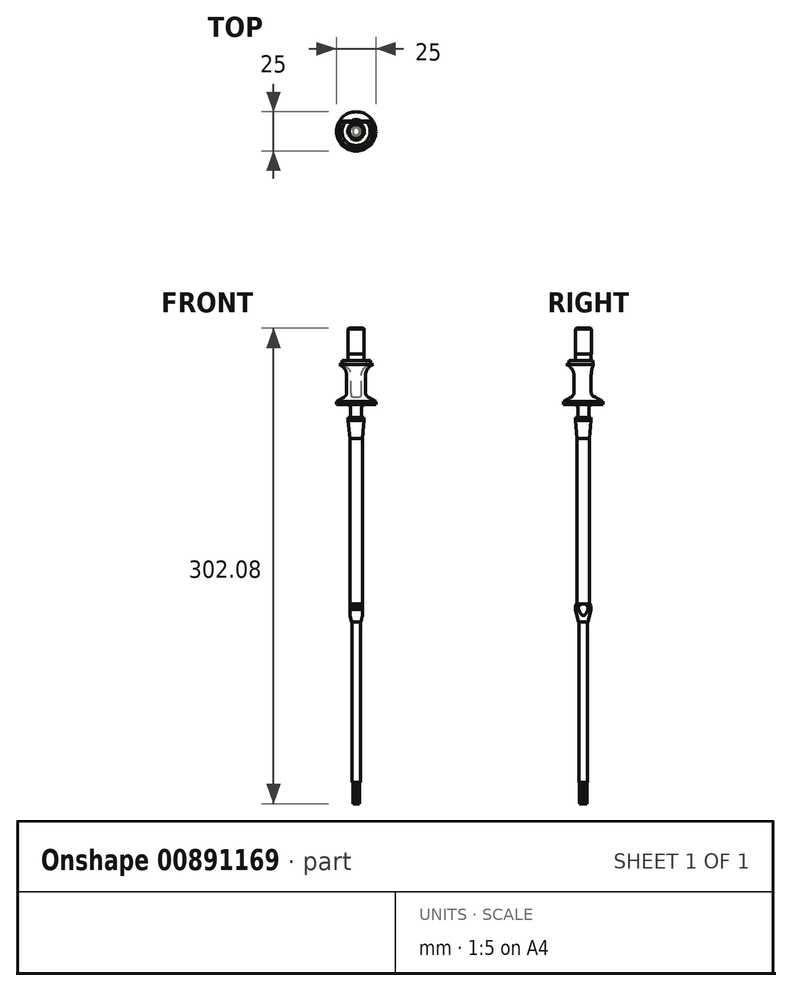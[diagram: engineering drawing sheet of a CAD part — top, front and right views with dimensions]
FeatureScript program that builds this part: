
annotation { "Feature Type Name" : "Feature", "Feature Type Description" : "" }
export const myFeature = defineFeature(function(context is Context, id is Id, definition is map)
    precondition{}
    {
        {
            var Q0;
            Q0=qCreatedBy(makeId("Front.planeOp"),FACE);
            var sketch = newSketch(context, id + "F0", { "sketchPlane" : qUnion([Q0])});
            skLineSegment(sketch, "E0.bottom", {"start": v(0, 218.5) * mm, "end": v(4, 218.5) * mm});
            skLineSegment(sketch, "E0.top", {"start": v(0, 113.5) * mm, "end": v(4, 113.5) * mm});
            skLineSegment(sketch, "E0.left", {"start": v(0, 218.5) * mm, "end": v(0, 113.5) * mm});
            skLineSegment(sketch, "E0.right", {"start": v(4, 218.5) * mm, "end": v(4, 113.5) * mm});
            skLineSegment(sketch, "E1", {"start": v(0, 230) * mm, "end": v(5, 230) * mm});
            skLineSegment(sketch, "E2", {"start": v(4, 218.5) * mm, "end": v(5, 230) * mm});
            skLineSegment(sketch, "E3", {"start": v(0, 230) * mm, "end": v(0, 218.5) * mm});
            skLineSegment(sketch, "E4", {"start": v(0, 112) * mm, "end": v(5, 112) * mm});
            skLineSegment(sketch, "E5", {"start": v(0, 113.5) * mm, "end": v(0, 112) * mm});
            skLineSegment(sketch, "E6", {"start": v(5, 112) * mm, "end": v(5, 110) * mm});
            skLineSegment(sketch, "E7", {"start": v(4, 113.5) * mm, "end": v(5, 112) * mm});
            skLineSegment(sketch, "E8", {"start": v(0, 112) * mm, "end": v(0, 110) * mm});
            skLineSegment(sketch, "E9", {"start": v(0, 110) * mm, "end": v(5, 110) * mm});
            skLineSegment(sketch, "E10", {"start": v(0, 110) * mm, "end": v(0, 102) * mm});
            skLineSegment(sketch, "E11", {"start": v(0, 102) * mm, "end": v(3, 102) * mm});
            skLineSegment(sketch, "E12", {"start": v(5, 110) * mm, "end": v(3, 102) * mm});
            skLineSegment(sketch, "E13.bottom", {"start": v(0, 102) * mm, "end": v(2.7, 102) * mm});
            skLineSegment(sketch, "E13.top", {"start": v(0, 0) * mm, "end": v(2.7, 0) * mm});
            skLineSegment(sketch, "E13.left", {"start": v(0, 102) * mm, "end": v(0, 0) * mm});
            skLineSegment(sketch, "E13.right", {"start": v(2.7, 102) * mm, "end": v(2.7, 0) * mm});
            skLineSegment(sketch, "E14.top", {"start": v(0, 232) * mm, "end": v(5, 232) * mm});
            skLineSegment(sketch, "E14.left", {"start": v(0, 230) * mm, "end": v(0, 232) * mm});
            skLineSegment(sketch, "E14.right", {"start": v(5, 230) * mm, "end": v(5, 232) * mm});
            skLineSegment(sketch, "E15.bottom", {"start": v(0, 232) * mm, "end": v(3.5, 232) * mm});
            skLineSegment(sketch, "E15.top", {"start": v(0, 238) * mm, "end": v(3.5, 238) * mm});
            skLineSegment(sketch, "E15.left", {"start": v(0, 232) * mm, "end": v(0, 238) * mm});
            skLineSegment(sketch, "E15.right", {"start": v(3.5, 232) * mm, "end": v(3.5, 238) * mm});
            skLineSegment(sketch, "E16", {"start": v(0, 238) * mm, "end": v(0, 240) * mm});
            skLineSegment(sketch, "E17", {"start": v(0, 240) * mm, "end": v(12.5, 240) * mm});
            skLineSegment(sketch, "E18", {"start": v(12.5, 240) * mm, "end": v(12.5, 242) * mm});
            skLineSegment(sketch, "E19", {"start": v(12.5, 242) * mm, "end": v(0, 242) * mm});
            skLineSegment(sketch, "E20", {"start": v(0, 242) * mm, "end": v(0, 240) * mm});
            skLineSegment(sketch, "E21", {"start": v(0, 242) * mm, "end": v(0, 245) * mm});
            skLineSegment(sketch, "E22", {"start": v(0, 245) * mm, "end": v(7.46, 245) * mm});
            skLineSegment(sketch, "E23", {"start": v(7.46, 245) * mm, "end": v(12.5, 242) * mm});
            skLineSegment(sketch, "E24", {"start": v(0, 245) * mm, "end": v(0, 247.58) * mm});
            skLineSegment(sketch, "E25", {"start": v(0, 247.58) * mm, "end": v(6, 247.58) * mm});
            skLineSegment(sketch, "E26.top", {"start": v(0, 258.58) * mm, "end": v(6, 258.58) * mm});
            skLineSegment(sketch, "E26.left", {"start": v(0, 247.58) * mm, "end": v(0, 258.58) * mm});
            skLineSegment(sketch, "E26.right", {"start": v(6, 247.58) * mm, "end": v(6, 258.58) * mm});
            skLineSegment(sketch, "E27", {"start": v(0, 258.58) * mm, "end": v(0, 265.58) * mm});
            skLineSegment(sketch, "E28", {"start": v(0, 265.58) * mm, "end": v(11, 265.58) * mm});
            skArc(sketch, "E29", {"start": v(11, 265.58) * mm, "mid": v(7.38, 262.88) * mm, "end": v(6, 258.58) * mm});
            skArc(sketch, "E30", {"start": v(5.5, 240) * mm, "mid": v(4.09, 239.41) * mm, "end": v(3.5, 238) * mm});
            skArc(sketch, "E31", {"start": v(6, 247.58) * mm, "mid": v(6.4, 246.1) * mm, "end": v(7.46, 245) * mm});
            skLineSegment(sketch, "E32.bottom", {"start": v(0, 265.58) * mm, "end": v(8.98, 265.58) * mm});
            skLineSegment(sketch, "E32.top", {"start": v(0, 268.08) * mm, "end": v(8.98, 268.08) * mm});
            skLineSegment(sketch, "E32.left", {"start": v(0, 265.58) * mm, "end": v(0, 268.08) * mm});
            skLineSegment(sketch, "E32.right", {"start": v(8.98, 265.58) * mm, "end": v(8.98, 268.08) * mm});
            skLineSegment(sketch, "E33.bottom", {"start": v(0, 268.08) * mm, "end": v(5, 268.08) * mm});
            skLineSegment(sketch, "E33.top", {"start": v(0, 272.08) * mm, "end": v(5, 272.08) * mm});
            skLineSegment(sketch, "E33.left", {"start": v(0, 268.08) * mm, "end": v(0, 272.08) * mm});
            skLineSegment(sketch, "E33.right", {"start": v(5, 268.08) * mm, "end": v(5, 272.08) * mm});
            skLineSegment(sketch, "E34.bottom", {"start": v(0, 272.08) * mm, "end": v(5.13, 272.08) * mm});
            skLineSegment(sketch, "E34.top", {"start": v(0, 288.08) * mm, "end": v(5.13, 288.08) * mm});
            skLineSegment(sketch, "E34.left", {"start": v(0, 272.08) * mm, "end": v(0, 288.08) * mm});
            skLineSegment(sketch, "E34.right", {"start": v(5.13, 272.08) * mm, "end": v(5.13, 288.08) * mm});
            skLineSegment(sketch, "E35", {"start": v(0, 288.08) * mm, "end": v(0, 288.58) * mm});
            skLineSegment(sketch, "E36", {"start": v(0, 288.58) * mm, "end": v(4.5, 288.58) * mm});
            skLineSegment(sketch, "E37", {"start": v(4.5, 288.58) * mm, "end": v(5.12, 288.08) * mm});
            skSolve(sketch);
        }
        {
            var Q0;
            Q0 = qSketchRegion(id + "F0", true);
            var Q1;
            Q1=sQuery(id+"F0.wireOp",EDGE,"E0.left");
            revolve(context, id + "F1", {"surfaceOperationType" : NewSurfaceOperationType.NEW, "entities" : qUnion([Q0]), "axis" : qUnion([Q1]), "revolveType" : RevolveType.FULL});
        }
        {
            var Q0;
            Q0=qCreatedBy(makeId("Front.planeOp"),FACE);
            var sketch = newSketch(context, id + "F2", { "sketchPlane" : qUnion([Q0])});
            skLineSegment(sketch, "E38.bottom", {"start": v(-4, 113.5) * mm, "end": v(-8, 113.5) * mm});
            skLineSegment(sketch, "E38.top", {"start": v(-4, 102) * mm, "end": v(-8, 102) * mm});
            skLineSegment(sketch, "E38.left", {"start": v(-4, 113.5) * mm, "end": v(-4, 102) * mm});
            skLineSegment(sketch, "E38.right", {"start": v(-8, 113.5) * mm, "end": v(-8, 102) * mm});
            skLineSegment(sketch, "E39.bottom", {"start": v(4, 113.5) * mm, "end": v(8, 113.5) * mm});
            skLineSegment(sketch, "E39.top", {"start": v(4, 102) * mm, "end": v(8, 102) * mm});
            skLineSegment(sketch, "E39.left", {"start": v(4, 113.5) * mm, "end": v(4, 102) * mm});
            skLineSegment(sketch, "E39.right", {"start": v(8, 113.5) * mm, "end": v(8, 102) * mm});
            skLineSegment(sketch, "E40", {"start": v(-4, 113.5) * mm, "end": v(-4, 218.5) * mm});
            skLineSegment(sketch, "E41", {"start": v(-4, 218.5) * mm, "end": v(-5, 230) * mm});
            skLineSegment(sketch, "E42.0", {"start": v(-4, 218.5) * mm, "end": v(4, 218.5) * mm});
            skLineSegment(sketch, "E43", {"start": v(-5, 110) * mm, "end": v(-5, 112) * mm});
            skSolve(sketch);
        }
        {
            var Q0;
            Q0=makeQuery(id+"F2.imprint","IMPRINT",FACE,{"disambiguationData":[TD([[makeQuery(id+"F2.imprint","IMPRINT",EDGE,{"derivedFrom":sQuery(id+"F2.wireOp",EDGE,"E38.bottom")}),1.0]])]});
            var Q1;
            Q1=makeQuery(id+"F2.imprint","IMPRINT",FACE,{"disambiguationData":[TD([[makeQuery(id+"F2.imprint","IMPRINT",EDGE,{"derivedFrom":sQuery(id+"F2.wireOp",EDGE,"E39.bottom")}),-1.0]])]});
            extrude(context, id + "F3", {"entities" : qUnion([Q0, Q1]), "operationType" : NewBodyOperationType.REMOVE, "oppositeDirection" : true, "depth" : 25 * mm, "offsetDistance" : 25 * mm, "hasSecondDirection" : true, "secondDirectionOppositeDirection" : false, "secondDirectionDepth" : 25 * mm});
        }
        {
            var Q0;
            Q0=qCreatedBy(makeId("Right.planeOp"),FACE);
            var sketch = newSketch(context, id + "F4", { "sketchPlane" : qUnion([Q0])});
            skLineSegment(sketch, "E44.bottom", {"start": v(6, 258.58) * mm, "end": v(5, 258.58) * mm});
            skLineSegment(sketch, "E44.top", {"start": v(6, 247.58) * mm, "end": v(5, 247.58) * mm});
            skLineSegment(sketch, "E44.left", {"start": v(6, 258.58) * mm, "end": v(6, 247.58) * mm});
            skLineSegment(sketch, "E44.right", {"start": v(5, 258.58) * mm, "end": v(5, 247.58) * mm});
            skLineSegment(sketch, "E45", {"start": v(0, 0) * mm, "end": v(0, 308.45) * mm, "construction": true});
            skArc(sketch, "E46", {"start": v(6.5, 265.58) * mm, "mid": v(5.38, 262.16) * mm, "end": v(5, 258.58) * mm});
            skLineSegment(sketch, "E47", {"start": v(6.5, 265.58) * mm, "end": v(13.4, 265.58) * mm});
            skLineSegment(sketch, "E48", {"start": v(13.4, 265.58) * mm, "end": v(7.46, 259.96) * mm});
            skLineSegment(sketch, "E49.bottom", {"start": v(0, 218.5) * mm, "end": v(4, 218.5) * mm});
            skLineSegment(sketch, "E49.top", {"start": v(0, 113.5) * mm, "end": v(4, 113.5) * mm});
            skLineSegment(sketch, "E49.left", {"start": v(0, 218.5) * mm, "end": v(0, 113.5) * mm});
            skLineSegment(sketch, "E49.right", {"start": v(4, 218.5) * mm, "end": v(4, 113.5) * mm});
            skLineSegment(sketch, "E50", {"start": v(0, 230) * mm, "end": v(5, 230) * mm});
            skLineSegment(sketch, "E51", {"start": v(4, 218.5) * mm, "end": v(5, 230) * mm});
            skLineSegment(sketch, "E52", {"start": v(0, 230) * mm, "end": v(0, 218.5) * mm});
            skLineSegment(sketch, "E53", {"start": v(0, 112) * mm, "end": v(5, 112) * mm});
            skLineSegment(sketch, "E54", {"start": v(0, 113.5) * mm, "end": v(0, 112) * mm});
            skLineSegment(sketch, "E55", {"start": v(5, 112) * mm, "end": v(5, 110) * mm});
            skLineSegment(sketch, "E56", {"start": v(4, 113.5) * mm, "end": v(5, 112) * mm});
            skLineSegment(sketch, "E57", {"start": v(0, 112) * mm, "end": v(0, 110) * mm});
            skLineSegment(sketch, "E58", {"start": v(0, 110) * mm, "end": v(5, 110) * mm});
            skLineSegment(sketch, "E59", {"start": v(0, 110) * mm, "end": v(0, 102) * mm});
            skLineSegment(sketch, "E60", {"start": v(0, 102) * mm, "end": v(3, 102) * mm});
            skLineSegment(sketch, "E61", {"start": v(5, 110) * mm, "end": v(3, 102) * mm});
            skLineSegment(sketch, "E62.top", {"start": v(0, 0) * mm, "end": v(3, 0) * mm});
            skLineSegment(sketch, "E62.left", {"start": v(0, 102) * mm, "end": v(0, 0) * mm});
            skLineSegment(sketch, "E62.right", {"start": v(3, 102) * mm, "end": v(3, 0) * mm});
            skLineSegment(sketch, "E63.top", {"start": v(0, 232) * mm, "end": v(5, 232) * mm});
            skLineSegment(sketch, "E63.left", {"start": v(0, 230) * mm, "end": v(0, 232) * mm});
            skLineSegment(sketch, "E63.right", {"start": v(5, 230) * mm, "end": v(5, 232) * mm});
            skLineSegment(sketch, "E64.bottom", {"start": v(0, 232) * mm, "end": v(3.5, 232) * mm});
            skLineSegment(sketch, "E64.top", {"start": v(0, 238) * mm, "end": v(3.5, 238) * mm});
            skLineSegment(sketch, "E64.left", {"start": v(0, 232) * mm, "end": v(0, 238) * mm});
            skLineSegment(sketch, "E64.right", {"start": v(3.5, 232) * mm, "end": v(3.5, 238) * mm});
            skLineSegment(sketch, "E65", {"start": v(0, 238) * mm, "end": v(0, 240) * mm});
            skLineSegment(sketch, "E66", {"start": v(0, 240) * mm, "end": v(12.5, 240) * mm});
            skLineSegment(sketch, "E67", {"start": v(12.5, 240) * mm, "end": v(12.5, 242) * mm});
            skLineSegment(sketch, "E68", {"start": v(12.5, 242) * mm, "end": v(0, 242) * mm});
            skLineSegment(sketch, "E69", {"start": v(0, 242) * mm, "end": v(0, 240) * mm});
            skLineSegment(sketch, "E70", {"start": v(0, 242) * mm, "end": v(0, 245) * mm});
            skLineSegment(sketch, "E71", {"start": v(0, 245) * mm, "end": v(7.46, 245) * mm});
            skLineSegment(sketch, "E72", {"start": v(7.46, 245) * mm, "end": v(12.5, 242) * mm});
            skLineSegment(sketch, "E73", {"start": v(0, 245) * mm, "end": v(0, 247.58) * mm});
            skLineSegment(sketch, "E74", {"start": v(0, 247.58) * mm, "end": v(6, 247.58) * mm});
            skLineSegment(sketch, "E75.top", {"start": v(0, 258.58) * mm, "end": v(6, 258.58) * mm});
            skLineSegment(sketch, "E75.left", {"start": v(0, 247.58) * mm, "end": v(0, 258.58) * mm});
            skLineSegment(sketch, "E75.right", {"start": v(6, 247.58) * mm, "end": v(6, 258.58) * mm});
            skLineSegment(sketch, "E76", {"start": v(0, 258.58) * mm, "end": v(0, 265.58) * mm});
            skLineSegment(sketch, "E77", {"start": v(0, 265.58) * mm, "end": v(11, 265.58) * mm});
            skArc(sketch, "E78", {"start": v(11, 265.58) * mm, "mid": v(7.38, 262.88) * mm, "end": v(6, 258.58) * mm});
            skLineSegment(sketch, "E79.bottom", {"start": v(0, 265.58) * mm, "end": v(3.5, 265.58) * mm});
            skLineSegment(sketch, "E79.top", {"start": v(0, 280.58) * mm, "end": v(3.5, 280.58) * mm});
            skLineSegment(sketch, "E79.left", {"start": v(0, 265.58) * mm, "end": v(0, 280.58) * mm});
            skLineSegment(sketch, "E79.right", {"start": v(3.5, 265.58) * mm, "end": v(3.5, 280.58) * mm});
            skArc(sketch, "E80", {"start": v(5.5, 240) * mm, "mid": v(4.09, 239.41) * mm, "end": v(3.5, 238) * mm});
            skArc(sketch, "E81", {"start": v(6, 247.58) * mm, "mid": v(6.4, 246.1) * mm, "end": v(7.46, 245) * mm});
            skArc(sketch, "E82", {"start": v(5, 247.58) * mm, "mid": v(5.72, 245.8) * mm, "end": v(7.46, 245) * mm});
            skLineSegment(sketch, "E83", {"start": v(7.46, 245) * mm, "end": v(7.46, 259.96) * mm});
            skLineSegment(sketch, "E84.bottom", {"start": v(6.5, 265.58) * mm, "end": v(11.23, 265.58) * mm});
            skLineSegment(sketch, "E84.top", {"start": v(6.5, 269.27) * mm, "end": v(11.23, 269.27) * mm});
            skLineSegment(sketch, "E84.left", {"start": v(6.5, 265.58) * mm, "end": v(6.5, 269.27) * mm, "construction": true});
            skLineSegment(sketch, "E84.right", {"start": v(11.23, 265.58) * mm, "end": v(11.23, 269.27) * mm});
            skLineSegment(sketch, "E85.top", {"start": v(6.5, 265.58) * mm, "end": v(6, 265.58) * mm});
            skLineSegment(sketch, "E86.top", {"start": v(6.5, 269.27) * mm, "end": v(6, 269.27) * mm});
            skLineSegment(sketch, "E86.left", {"start": v(6.5, 265.58) * mm, "end": v(6.5, 269.27) * mm});
            skLineSegment(sketch, "E86.right", {"start": v(6, 265.58) * mm, "end": v(6, 269.27) * mm});
            skSolve(sketch);
        }
        {
            var Q0;
            {var subQ5=sQuery(id+"F4.wireOp",EDGE,"E78");Q0=makeQuery(id+"F4.imprint","IMPRINT",FACE,{"disambiguationData":[TD([[makeQuery(id+"F4.imprint","IMPRINT",EDGE,{"derivedFrom":subQ5}),-1.0]])]});}
            var Q1;
            {var subQ0=sQuery(id+"F4.wireOp",EDGE,"E44.right");Q1=makeQuery(id+"F4.imprint","IMPRINT",FACE,{"disambiguationData":[TD([[makeQuery(id+"F4.imprint","IMPRINT",EDGE,{"derivedFrom":subQ0}),1.0]])]});}
            var Q2;
            {var subQ2=sQuery(id+"F4.wireOp",EDGE,"E81");Q2=makeQuery(id+"F4.imprint","IMPRINT",FACE,{"disambiguationData":[TD([[makeQuery(id+"F4.imprint","IMPRINT",EDGE,{"derivedFrom":subQ2}),-1.0]])]});}
            var Q3;
            {var subQ6=sQuery(id+"F4.wireOp",EDGE,"dJMTZFCG-ALeP-d3n5-IoNv-8sD2kWQqoZ35.top");Q3=makeQuery(id+"F4.imprint","IMPRINT",FACE,{"disambiguationData":[TD([[makeQuery(id+"F4.imprint","IMPRINT",EDGE,{"derivedFrom":subQ6}),-1.0]])]});}
            var Q4;
            {var subQ5=sQuery(id+"F4.wireOp",EDGE,"E84.top");Q4=makeQuery(id+"F4.imprint","IMPRINT",FACE,{"disambiguationData":[TD([[makeQuery(id+"F4.imprint","IMPRINT",EDGE,{"derivedFrom":subQ5}),-1.0]])]});}
            var Q5;
            Q5=makeQuery(id+"F4.imprint","IMPRINT",FACE,{"disambiguationData":[TD([[makeQuery(id+"F4.imprint","IMPRINT",EDGE,{"derivedFrom":sQuery(id+"F4.wireOp",EDGE,"E85.top")}),-1.0]])]});
            extrude(context, id + "F5", {"entities" : qUnion([Q0, Q1, Q2, Q3, Q4, Q5]), "operationType" : NewBodyOperationType.REMOVE, "depth" : 25 * mm, "offsetDistance" : 25 * mm, "hasSecondDirection" : true, "secondDirectionOppositeDirection" : true, "secondDirectionDepth" : 25 * mm});
        }
        {
            var Q0;
            Q0=makeQuery(id+"F1.opRevolve","SWEPT_FACE",FACE,{"disambiguationData":[OSD([sQuery(id+"F0.wireOp",EDGE,"E13.top")])]});
            cPlane(context, id + "F6", {"entities" : qUnion([Q0]), "cplaneType" : CPlaneType.OFFSET, "offset" : 0 * mm, "width" : 150 * mm, "height" : 150 * mm});
        }
        {
            var Q0;
            Q0=qCreatedBy(id+"F6.planeOp",FACE);
            var sketch = newSketch(context, id + "F7", { "sketchPlane" : qUnion([Q0])});
            skLineSegment(sketch, "E87", {"start": v(0, 0) * mm, "end": v(8.93, 0) * mm, "construction": true});
            skCircle(sketch, "E88.cCircle", {"center": v(0, 0) * mm, "radius": 2 * mm, "construction": true});
            skLineSegment(sketch, "E88.0", {"start": v(0, 2.3) * mm, "end": v(2, 1.15) * mm});
            skLineSegment(sketch, "E88.1", {"start": v(2, 1.15) * mm, "end": v(2, -1.15) * mm});
            skLineSegment(sketch, "E88.2", {"start": v(2, -1.15) * mm, "end": v(0, -2.3) * mm});
            skLineSegment(sketch, "E88.3", {"start": v(0, -2.3) * mm, "end": v(-2, -1.15) * mm});
            skLineSegment(sketch, "E88.4", {"start": v(-2, -1.15) * mm, "end": v(-2, 1.15) * mm});
            skLineSegment(sketch, "E88.5", {"start": v(-2, 1.15) * mm, "end": v(0, 2.3) * mm});
            skPoint(sketch, "E88.0.midPoint", {"position": v(1, 1.73) * mm});
            skLineSegment(sketch, "E89", {"start": v(0, 0) * mm, "end": v(1, 1.73) * mm, "construction": true});
            skSolve(sketch);
        }
        {
            var Q0;
            Q0=makeQuery(id+"F7.imprint","IMPRINT",FACE,{"disambiguationData":[TD([[makeQuery(id+"F7.imprint","IMPRINT",EDGE,{"derivedFrom":sQuery(id+"F7.wireOp",EDGE,"E88.0")}),-1.0]])]});
            extrude(context, id + "F8", {"entities" : qUnion([Q0]), "operationType" : NewBodyOperationType.ADD, "depth" : 13.5 * mm, "offsetDistance" : 25 * mm});
        }
    });
